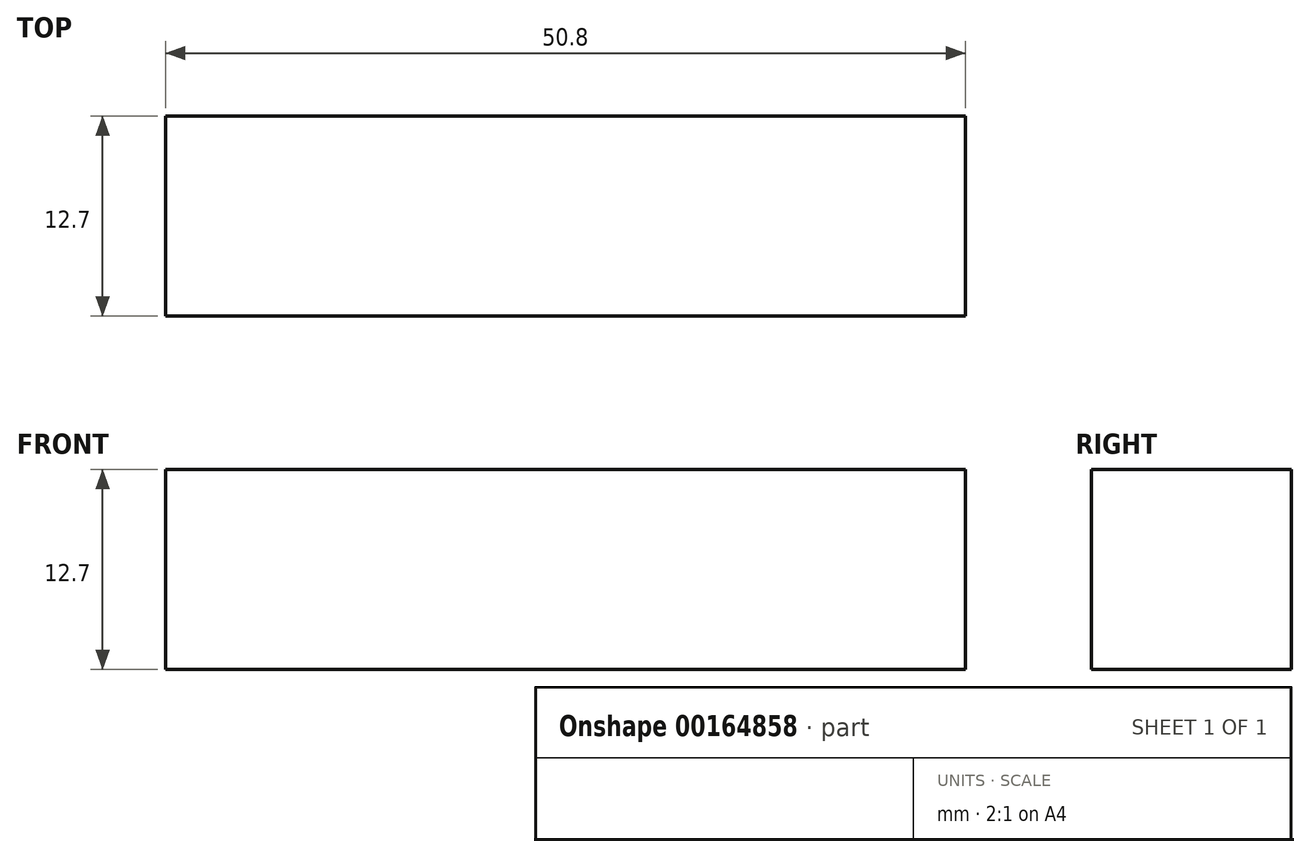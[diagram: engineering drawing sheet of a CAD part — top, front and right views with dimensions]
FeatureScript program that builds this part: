
annotation { "Feature Type Name" : "Feature", "Feature Type Description" : "" }
export const myFeature = defineFeature(function(context is Context, id is Id, definition is map)
    precondition{}
    {
        {
            var Q0;
            Q0=qCreatedBy(makeId("Top.planeOp"),FACE);
            var sketch = newSketch(context, id + "F0", { "sketchPlane" : qUnion([Q0])});
            skLineSegment(sketch, "E0.bottom", {"start": v(0, 0) * mm, "end": v(50.8, 0) * mm});
            skLineSegment(sketch, "E0.top", {"start": v(0, -12.7) * mm, "end": v(50.8, -12.7) * mm});
            skLineSegment(sketch, "E0.left", {"start": v(0, 0) * mm, "end": v(0, -12.7) * mm});
            skLineSegment(sketch, "E0.right", {"start": v(50.8, 0) * mm, "end": v(50.8, -12.7) * mm});
            skSolve(sketch);
        }
        {
            var Q0;
            Q0 = qSketchRegion(id + "F0", true);
            extrude(context, id + "F1", {"entities" : qUnion([Q0]), "depth" : 12.7 * mm});
        }
    });
